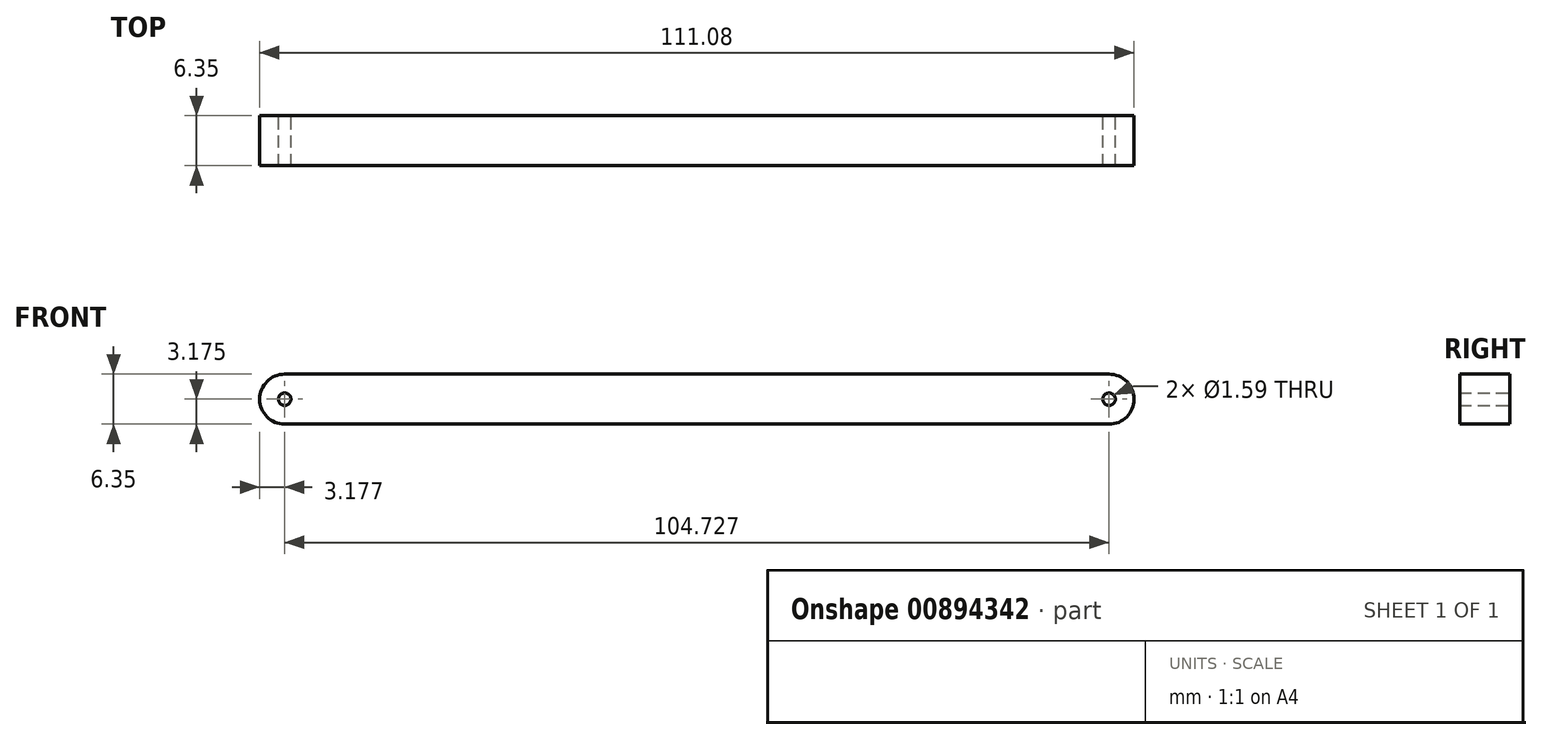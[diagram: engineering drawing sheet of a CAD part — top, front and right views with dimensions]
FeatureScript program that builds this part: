
annotation { "Feature Type Name" : "Feature", "Feature Type Description" : "" }
export const myFeature = defineFeature(function(context is Context, id is Id, definition is map)
    precondition{}
    {
        {
            var Q0;
            Q0=qCreatedBy(makeId("Front.planeOp"),FACE);
            var sketch = newSketch(context, id + "F0", { "sketchPlane" : qUnion([Q0])});
            skLineSegment(sketch, "E0.bottom", {"start": v(-55.54, 6.35) * mm, "end": v(55.54, 6.35) * mm});
            skLineSegment(sketch, "E0.top", {"start": v(-55.54, 0) * mm, "end": v(55.54, 0) * mm});
            skLineSegment(sketch, "E0.left", {"start": v(-55.54, 6.35) * mm, "end": v(-55.54, 0) * mm});
            skLineSegment(sketch, "E0.right", {"start": v(55.54, 6.35) * mm, "end": v(55.54, 0) * mm});
            skCircle(sketch, "E1", {"center": v(-52.36, 3.17) * mm, "radius": 0.8 * mm});
            skCircle(sketch, "E2.MirrorC", {"center": v(52.36, 3.17) * mm, "radius": 0.8 * mm});
            skSolve(sketch);
        }
        {
            var Q0;
            Q0=makeQuery(id+"F0.imprint","IMPRINT",FACE,{"disambiguationData":[TD([[makeQuery(id+"F0.imprint","IMPRINT",EDGE,{"derivedFrom":sQuery(id+"F0.wireOp",EDGE,"E0.bottom")}),-1.0]])]});
            extrude(context, id + "F1", {"entities" : qUnion([Q0]), "depth" : 6.35 * mm, "offsetDistance" : 25.4 * mm});
        }
        {
            var Q0;
            Q0=makeQuery(id+"F1.opExtrude","SWEPT_EDGE",EDGE,{"disambiguationData":[OSD([sQuery(id+"F0.wireOp",EDGE,"E0.bottom"),sQuery(id+"F0.wireOp",EDGE,"E0.right")])]});
            var Q1;
            Q1=makeQuery(id+"F1.opExtrude","SWEPT_EDGE",EDGE,{"disambiguationData":[OSD([sQuery(id+"F0.wireOp",EDGE,"E0.top"),sQuery(id+"F0.wireOp",EDGE,"E0.right")])]});
            var Q2;
            Q2=makeQuery(id+"F1.opExtrude","SWEPT_EDGE",EDGE,{"disambiguationData":[OSD([sQuery(id+"F0.wireOp",EDGE,"E0.bottom"),sQuery(id+"F0.wireOp",EDGE,"E0.left")])]});
            var Q3;
            Q3=makeQuery(id+"F1.opExtrude","SWEPT_EDGE",EDGE,{"disambiguationData":[OSD([sQuery(id+"F0.wireOp",EDGE,"E0.top"),sQuery(id+"F0.wireOp",EDGE,"E0.left")])]});
            fillet(context, id + "F2", {"entities" : qUnion([Q0, Q1, Q2, Q3]), "radius" : 3.17 * mm, "tangentPropagation" : true, "allowEdgeOverflow" : false});
        }
    });
